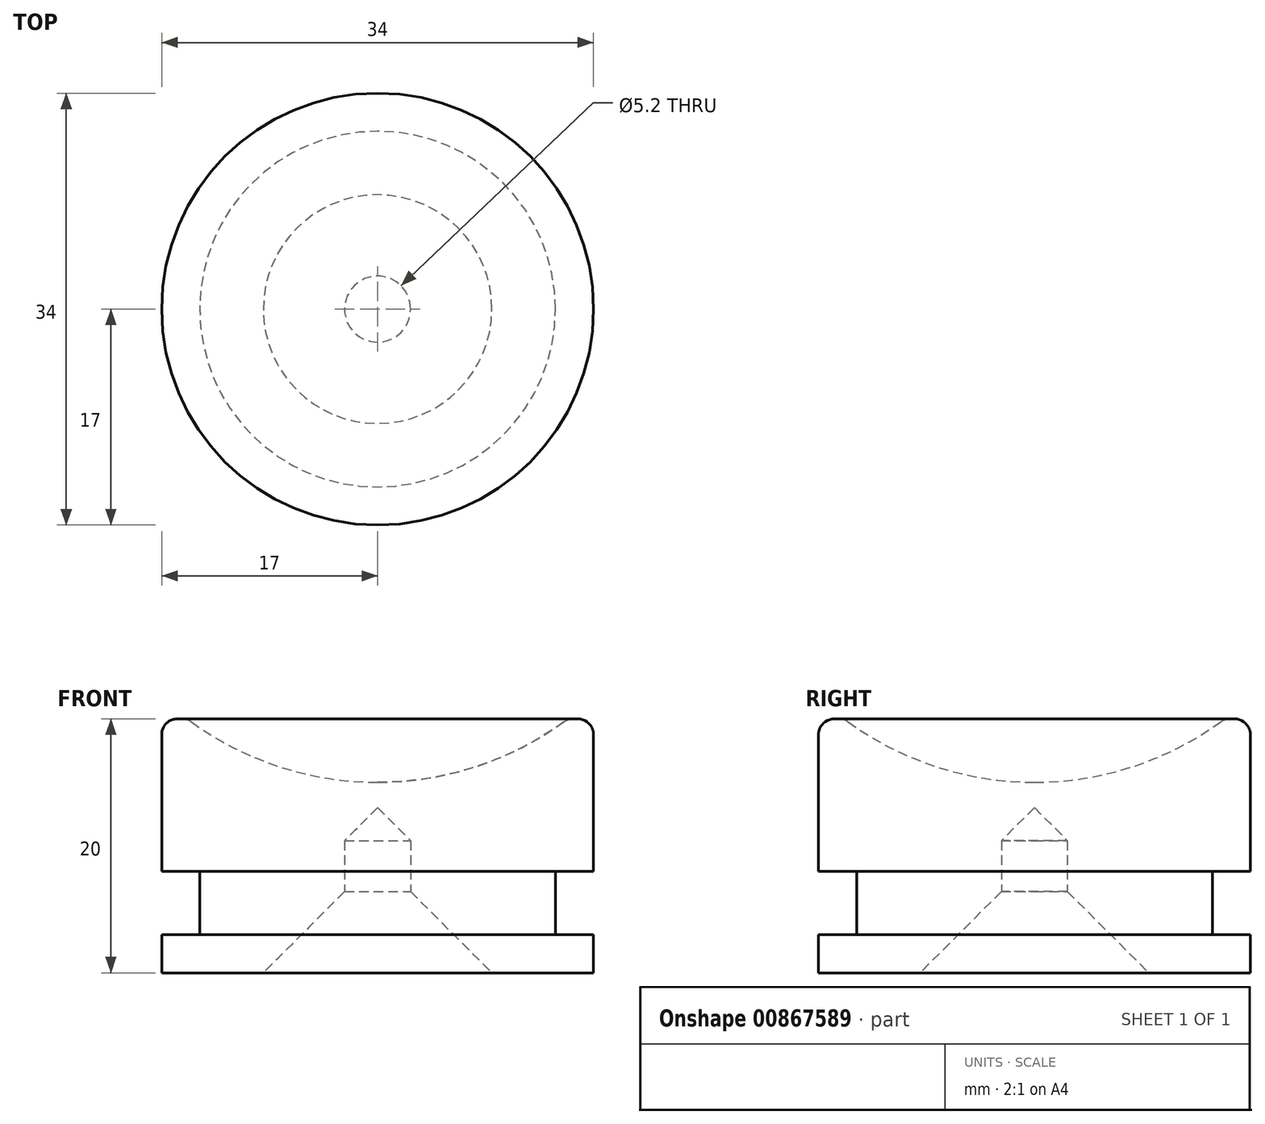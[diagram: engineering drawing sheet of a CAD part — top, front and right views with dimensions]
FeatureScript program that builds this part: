
annotation { "Feature Type Name" : "Feature", "Feature Type Description" : "" }
export const myFeature = defineFeature(function(context is Context, id is Id, definition is map)
    precondition{}
    {
        {
            var Q0;
            Q0=qCreatedBy(makeId("Front.planeOp"),FACE);
            var sketch = newSketch(context, id + "F0", { "sketchPlane" : qUnion([Q0])});
            skLineSegment(sketch, "E0", {"start": v(0, 0) * mm, "end": v(0, 15) * mm, "construction": true});
            skLineSegment(sketch, "E1", {"start": v(17, 15) * mm, "end": v(0, 15) * mm, "construction": true});
            skArc(sketch, "E2", {"start": v(0, 15) * mm, "mid": v(7.72, 16.22) * mm, "end": v(14.68, 19.76) * mm});
            skLineSegment(sketch, "E3", {"start": v(15.41, 20) * mm, "end": v(15.75, 20) * mm});
            skLineSegment(sketch, "E4", {"start": v(17, 18.75) * mm, "end": v(17, 8) * mm});
            skLineSegment(sketch, "E5", {"start": v(17, 8) * mm, "end": v(14, 8) * mm});
            skLineSegment(sketch, "E6", {"start": v(14, 8) * mm, "end": v(14, 3) * mm});
            skLineSegment(sketch, "E7", {"start": v(14, 3) * mm, "end": v(17, 3) * mm});
            skLineSegment(sketch, "E8", {"start": v(17, 3) * mm, "end": v(17, 0) * mm});
            skPoint(sketch, "E9.visualSharp", {"position": v(15, 20) * mm});
            skArc(sketch, "E9.filletArc", {"start": v(15.41, 20) * mm, "mid": v(15.03, 19.94) * mm, "end": v(14.68, 19.76) * mm});
            skPoint(sketch, "E10.visualSharp", {"position": v(17, 20) * mm});
            skArc(sketch, "E10.filletArc", {"start": v(17, 18.75) * mm, "mid": v(16.63, 19.63) * mm, "end": v(15.75, 20) * mm});
            skLineSegment(sketch, "E11", {"start": v(0, 15) * mm, "end": v(0, 13) * mm});
            skPoint(sketch, "E12.end.orphan", {"position": v(14, 0) * mm});
            skLineSegment(sketch, "E13", {"start": v(17, 0) * mm, "end": v(9, 0) * mm});
            skLineSegment(sketch, "E14", {"start": v(9, 0) * mm, "end": v(2.6, 6.4) * mm});
            skLineSegment(sketch, "E15", {"start": v(2.6, 6.4) * mm, "end": v(2.6, 10.4) * mm});
            skLineSegment(sketch, "E16", {"start": v(2.6, 10.4) * mm, "end": v(0, 13) * mm});
            skSolve(sketch);
        }
        {
            var Q0;
            Q0 = qSketchRegion(id + "F0", true);
            var Q1;
            Q1=sQuery(id+"F0.wireOp",EDGE,"E0");
            revolve(context, id + "F1", {"surfaceOperationType" : NewSurfaceOperationType.NEW, "entities" : qUnion([Q0]), "axis" : qUnion([Q1]), "revolveType" : RevolveType.FULL});
        }
    });
